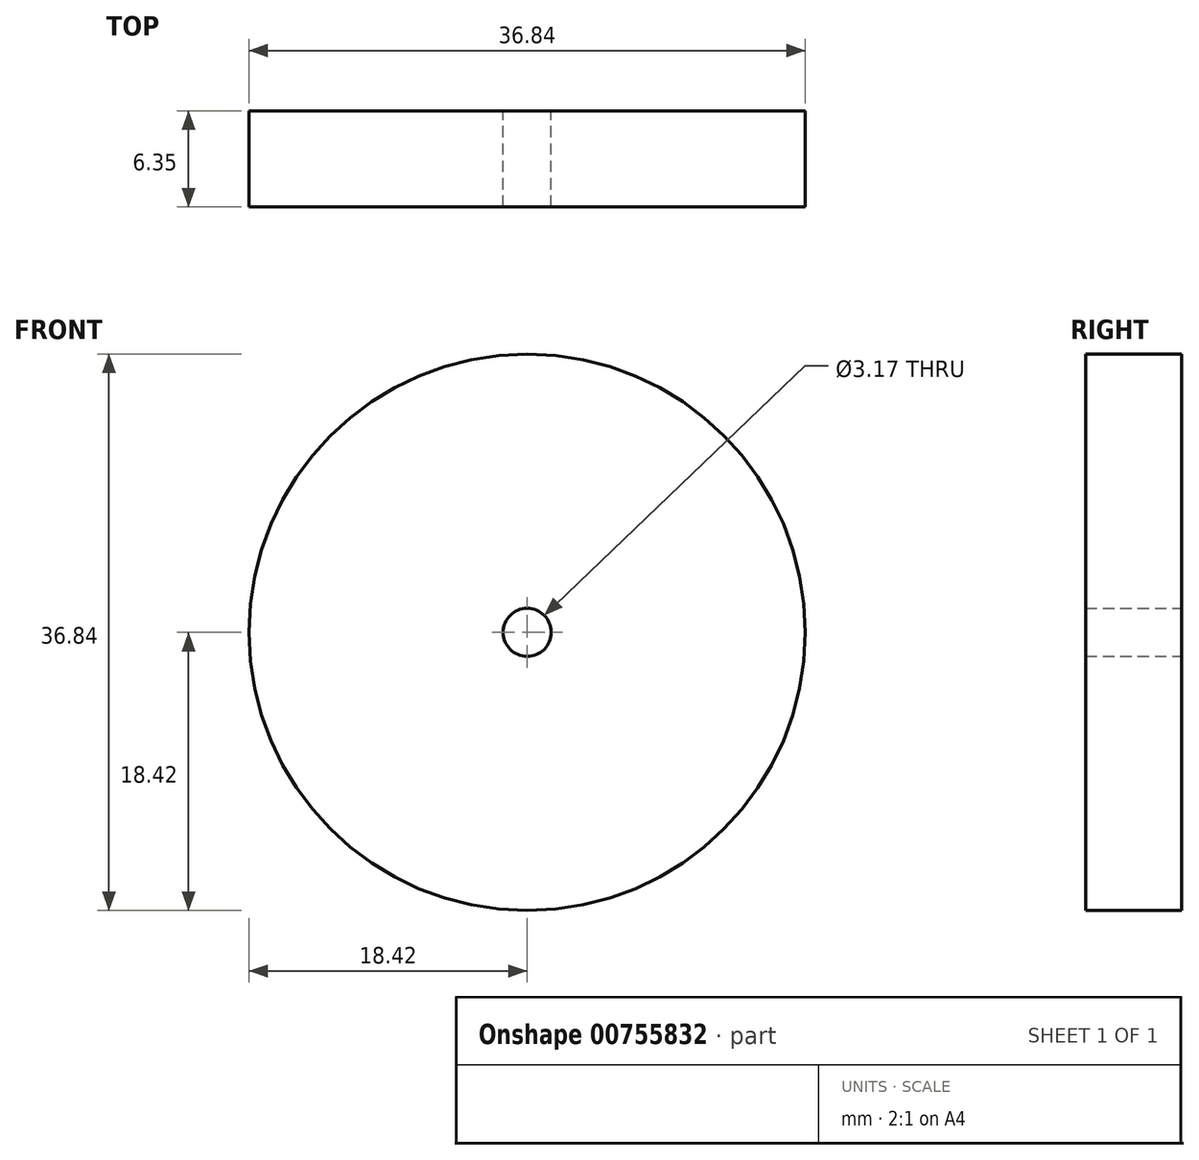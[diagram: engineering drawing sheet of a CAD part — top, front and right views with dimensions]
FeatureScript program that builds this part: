
annotation { "Feature Type Name" : "Feature", "Feature Type Description" : "" }
export const myFeature = defineFeature(function(context is Context, id is Id, definition is map)
    precondition{}
    {
        {
            var Q0;
            Q0=qCreatedBy(makeId("Front.planeOp"),FACE);
            var sketch = newSketch(context, id + "F0", { "sketchPlane" : qUnion([Q0])});
            skCircle(sketch, "E0", {"center": v(0, 0) * mm, "radius": 18.41 * mm});
            skCircle(sketch, "E1", {"center": v(0, 0) * mm, "radius": 1.59 * mm});
            skSolve(sketch);
        }
        {
            var Q0;
            Q0=qSketchRegion(id+"F0",true);
            extrude(context, id + "F1", {"entities" : qUnion([Q0]), "depth" : 6.35 * mm, "offsetDistance" : 25.4 * mm});
        }
    });
